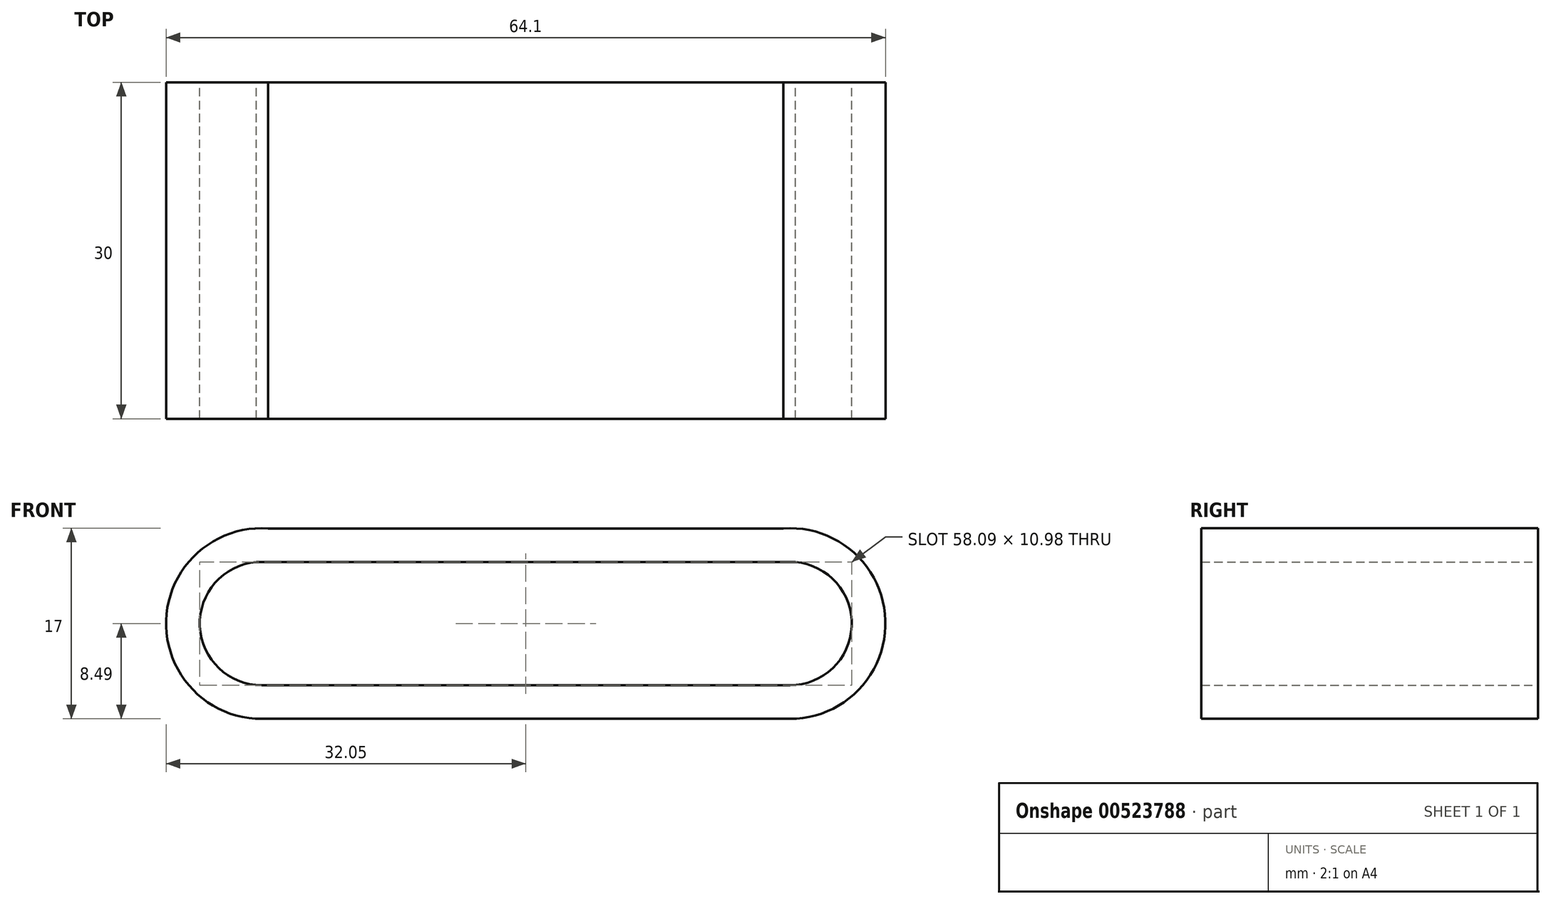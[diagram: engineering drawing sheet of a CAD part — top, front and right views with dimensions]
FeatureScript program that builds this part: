
annotation { "Feature Type Name" : "Feature", "Feature Type Description" : "" }
export const myFeature = defineFeature(function(context is Context, id is Id, definition is map)
    precondition{}
    {
        {
            var Q0;
            Q0=qCreatedBy(makeId("Front.planeOp"),FACE);
            var sketch = newSketch(context, id + "F0", { "sketchPlane" : qUnion([Q0])});
            skArc(sketch, "E0", {"start": v(-24.02, 5.48) * mm, "mid": v(-29.04, -0.24) * mm, "end": v(-23.54, -5.5) * mm});
            skLineSegment(sketch, "E1", {"start": v(0, 15.97) * mm, "end": v(0, -15.29) * mm, "construction": true});
            skLineSegment(sketch, "E2", {"start": v(-24.02, 5.48) * mm, "end": v(0, 5.48) * mm});
            skLineSegment(sketch, "E3", {"start": v(-23.54, -5.5) * mm, "end": v(0, -5.5) * mm});
            skLineSegment(sketch, "E4.0", {"start": v(-22.96, 8.48) * mm, "end": v(0, 8.48) * mm});
            skArc(sketch, "E4.1", {"start": v(-22.96, 8.48) * mm, "mid": v(-32.05, 0.29) * mm, "end": v(-23.53, -8.5) * mm});
            skLineSegment(sketch, "E4.2", {"start": v(-23.53, -8.5) * mm, "end": v(0.65, -8.5) * mm});
            skLineSegment(sketch, "E5.MirrorCS", {"start": v(22.96, 8.48) * mm, "end": v(0, 8.48) * mm});
            skLineSegment(sketch, "E6.MirrorCS", {"start": v(24.02, 5.48) * mm, "end": v(0, 5.48) * mm});
            skArc(sketch, "E7.MirrorCS", {"start": v(22.96, 8.48) * mm, "mid": v(32.05, 0.29) * mm, "end": v(23.53, -8.5) * mm});
            skArc(sketch, "E8.MirrorCS", {"start": v(24.02, 5.48) * mm, "mid": v(29.04, -0.24) * mm, "end": v(23.54, -5.5) * mm});
            skLineSegment(sketch, "E9.MirrorCS", {"start": v(23.54, -5.5) * mm, "end": v(0, -5.5) * mm});
            skLineSegment(sketch, "E10.MirrorCS", {"start": v(23.53, -8.5) * mm, "end": v(-0.65, -8.5) * mm});
            skSolve(sketch);
        }
        {
            var Q0;
            Q0=makeQuery(id+"F0.imprint","IMPRINT",FACE,{"disambiguationData":[TD([[makeQuery(id+"F0.imprint","IMPRINT",EDGE,{"derivedFrom":sQuery(id+"F0.wireOp",EDGE,"E0")}),-1.0]])]});
            extrude(context, id + "F1", {"entities" : qUnion([Q0]), "depth" : 30 * mm, "offsetDistance" : 25 * mm});
        }
    });
